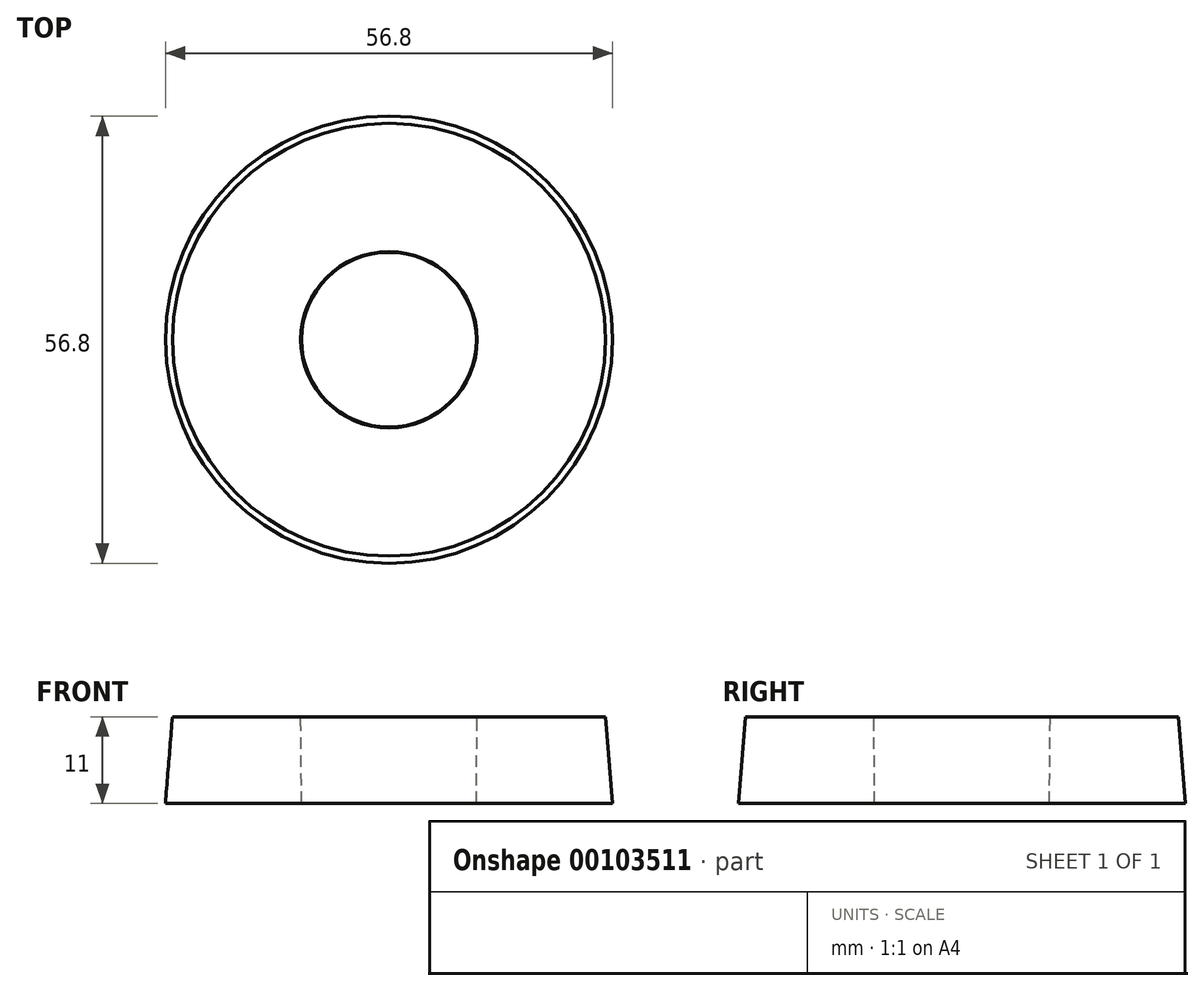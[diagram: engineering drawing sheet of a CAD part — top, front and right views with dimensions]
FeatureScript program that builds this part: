
annotation { "Feature Type Name" : "Feature", "Feature Type Description" : "" }
export const myFeature = defineFeature(function(context is Context, id is Id, definition is map)
    precondition{}
    {
        {
            var Q0;
            Q0=qCreatedBy(makeId("Front.planeOp"),FACE);
            var sketch = newSketch(context, id + "F0", { "sketchPlane" : qUnion([Q0])});
            skLineSegment(sketch, "E0", {"start": v(0, 0) * mm, "end": v(-11.1, 0) * mm, "construction": true});
            skLineSegment(sketch, "E1", {"start": v(-11.1, 0) * mm, "end": v(-28.4, 0) * mm});
            skLineSegment(sketch, "E2", {"start": v(-28.4, 0) * mm, "end": v(-27.5, 11) * mm});
            skLineSegment(sketch, "E3", {"start": v(-27.5, 11) * mm, "end": v(-11.2, 11) * mm});
            skLineSegment(sketch, "E4", {"start": v(-11.2, 11) * mm, "end": v(0, 11) * mm, "construction": true});
            skLineSegment(sketch, "E5", {"start": v(0, 0) * mm, "end": v(0, 11) * mm, "construction": true});
            skLineSegment(sketch, "E6", {"start": v(-11.2, 11) * mm, "end": v(-11.1, 0) * mm});
            skSolve(sketch);
        }
        {
            var Q0;
            Q0=makeQuery(id+"F0.imprint","IMPRINT",FACE,{"disambiguationData":[TD([[makeQuery(id+"F0.imprint","IMPRINT",EDGE,{"derivedFrom":sQuery(id+"F0.wireOp",EDGE,"E1")}),-1.0]])]});
            var Q1;
            Q1=sQuery(id+"F0.wireOp",EDGE,"E5");
            revolve(context, id + "F1", {"entities" : qUnion([Q0]), "axis" : qUnion([Q1]), "revolveType" : RevolveType.FULL});
        }
    });
